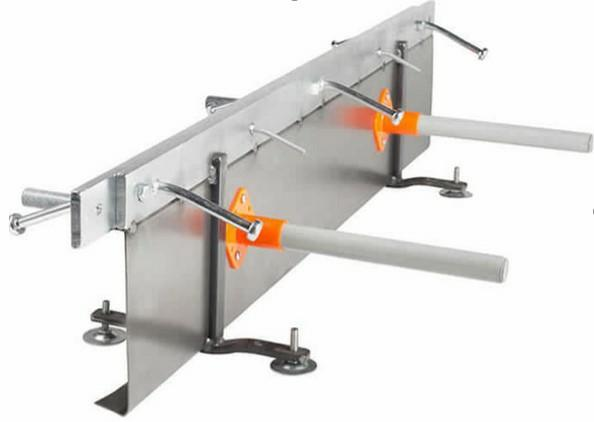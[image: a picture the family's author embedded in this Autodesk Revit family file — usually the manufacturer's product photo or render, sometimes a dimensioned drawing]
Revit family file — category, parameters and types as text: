
# Revit family: EOS RF Klassische Fugenprofile
name_source: partatom
category: Generic Models
units: mm (PartAtom-declared; Revit-internal decimal feet)

## family parameters
Always vertical = No
Can host rebar = No
Cut with Voids When Loaded = No
Part Type = Normal
Room Calculation Point = No
Round Connector Dimension = Use Diameter
Shared = No
Work Plane-Based = Yes

## types (5) — shared parameters
Adresse = Iglauer Str. 6 86316 Friedberg
Basismaterial EOS = Stahl S235 JR
Brandschutzklasse = XY
Description = Dehnfugen Tagesfeldabschalungen
Keynote = EOS
Lieferzeit = 2 Wochen
Manufacturer = Hersteller\Guggemos GmbH,
Model = Fugenprofile für Industriebodenplatten
Telefon = +49 (0)8 21 / 455 969 0
URL = https://www.fugenprofile.de
Video = https://www.youtube.com
zero-valued in all types: Default Elevation

## per-type parameters (varying)
| type | Abstand zu den Pips (h) | Anzahl der Rohre | Höhe | Länge | Startabstand zu Stützgestellen | Stufe der Stützgestelle | Type Comments | Type Image |
| EOS_RF_L3000_H450 | 215 mm | 6 | 450 mm  [stored 1.47638 ft] | 3000 mm  [stored 9.84252 ft] | 500 mm  [stored 1.64042 ft] | 3 | EOS_L3000 | Picture 1.jpg |
| EOS_RF_L2000_H450 | 215 mm | 4 | 450 mm  [stored 1.47638 ft] | 2000 mm  [stored 6.56168 ft] | 500 mm  [stored 1.64042 ft] | 2 | EOS_L2000 | Picture 1.jpg |
| EOS_RF_L4000_H500 | 240 mm  [stored 0.787402 ft] | 8 | 500 mm  [stored 1.64042 ft] | 4000 mm  [stored 13.1234 ft] | 500 mm  [stored 1.64042 ft] | 4 | EOS_L4000 | <None> |
| EOS_RF_L1000_H450 | 215 mm | 2 | 450 mm  [stored 1.47638 ft] | 1000 mm  [stored 3.28084 ft] | 0 mm  [stored 0 ft] | 2 | EOS_L1000 | Picture 1.jpg |
| EOS_RF_L4500_H500 | 240 mm  [stored 0.787402 ft] | 9 | 500 mm  [stored 1.64042 ft] | 4500 mm  [stored 14.7638 ft] | 500 mm  [stored 1.64042 ft] | 4 | EOS_L4500 | Picture 1.jpg |

note: [stored X ft] marks values corroborated as IEEE doubles in the binary element streams (Revit-internal decimal feet)

## geometry (parser evidence)
native form markers: Sweep x14
no freeform markers — native parametric forms only
